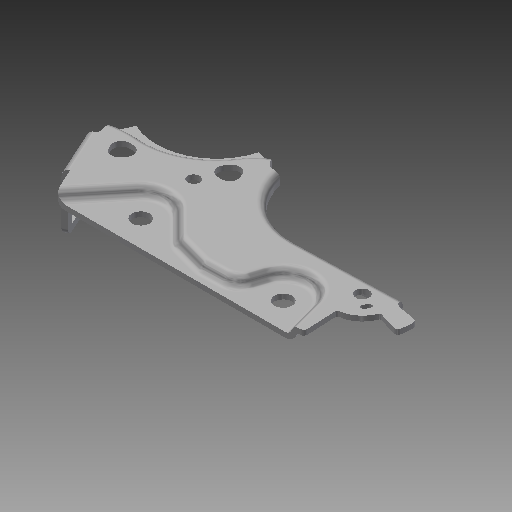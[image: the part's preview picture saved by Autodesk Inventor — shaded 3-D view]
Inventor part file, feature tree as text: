
AUTODESK INVENTOR PART (.ipt)
format: ipt  version: 2019 (Build 230136000, 136)  size: 795,648 bytes
history: native  units: mm
features: fillet x22, sketch x18, extrude x16, hole x2, plane x1, chamfer x1, other x1
ambient origin geometry x8: Origin, YZ Plane, XZ Plane, XY Plane, X Axis, Y Axis, Z Axis, Center Point
bodies: Solid1 (feature_tree)
feature tree (61):
  extrude  "Extrusion1"  Depth=24.072582mm
  fillet  "Fillet1"  Radius=40.0mm
  fillet  "Fillet2"  Radius=94.598888mm
  fillet  "Fillet3"  Radius=160.198557mm
  extrude  "Extrusion2"  Depth=96.114965mm
  fillet  "Fillet4"  Radius=10.045152mm
  extrude  "Extrusion3"  Depth=20.365459mm
  extrude  "Extrusion7"  Depth=45.416983mm
  extrude  "Extrusion8"  Depth=3.0mm
  fillet  "Fillet11"  Radius=22.488064mm
  fillet  "Fillet12"  Radius=151.434268mm
  fillet  "Fillet13"  Radius=3.0mm
  extrude  "Extrusion9"  Depth=2.0mm
  extrude  "Extrusion10"  Depth=4.0mm
  extrude  "Extrusion11"  Depth=79.045157mm
  fillet  "Fillet14"  Radius=32.0mm
  fillet  "Fillet15"  Radius=32.0mm
  fillet  "Fillet16"  Radius=60.0mm
  fillet  "Fillet18"  Radius=80.0mm
  extrude  "Extrusion12"  Depth=10.0mm
  fillet  "Fillet19"  Radius=83.0mm
  fillet  "Fillet20"  Radius=24.0mm
  fillet  "Fillet21"  Radius=95.0mm
  fillet  "Fillet22"  Radius=52.768526mm
  fillet  "Fillet23"  Radius=43.0mm
  extrude  "Extrusion13"  Depth=10.79818mm
  fillet  "Fillet25"  Radius=5.0mm
  extrude  "Extrusion14"  Depth=3.0mm
  fillet  "Fillet26"  Radius=21.0mm
  fillet  "Fillet27"  Radius=44.5mm
  fillet  "Fillet28"  Radius=3.0mm
  plane  "Work Plane2"
  hole  "Hole1"  [1 undecoded]
  extrude  "Extrusion15"  Depth=1.0mm
  extrude  "Extrusion16"  Depth=3.0mm
  extrude  "Extrusion17"  Depth=3.0mm
  fillet  "Fillet29"  Radius=3.0mm
  chamfer  "Chamfer1"  Distance=3.0mm
  hole  "Hole3"  [1 undecoded]
  extrude  "Extrusion18"  Depth=4.0mm
  fillet  "Fillet30"  Radius=2.0mm
  extrude  "Extrusion19"  Depth=10.0mm
  sketch  "Sketch2"  dims[d0=36.0mm d1=24.072582mm d2=40.0mm d3=94.598888mm d4=160.198557mm]
  sketch  "Sketch3"  dims[d5=72.17844mm d6=96.114965mm d7=10.045152mm]
  sketch  "Sketch4"  dims[d9=12.319886mm d10=20.365459mm]
  sketch  "Sketch9"  dims[d11=19.108732mm d12=45.416983mm]
  sketch  "Sketch10"  dims[d15=19.938804mm d16=17.317927mm d18=22.488064mm d19=151.434268mm d20=3.0mm d21=0.0mm]
  sketch  "Sketch11"  dims[d22=25.0mm d23=2.0mm]
  sketch  "Sketch12"  dims[d24=4.0mm d25=79.045157mm]
  sketch  "Sketch13"  dims[d26=33.682036mm d28=79.045157mm d29=32.0mm d30=32.0mm d33=60.0mm d34=80.0mm]
  sketch  "Sketch14"  dims[d36=5.0mm d37=0.0mm d38=10.0mm d41=83.0mm d42=24.0mm d43=95.0mm d45=52.768526mm d46=43.0mm]
  sketch  "Sketch15"  dims[d47=27.664247mm d48=10.79818mm d51=5.0mm d52=0.0mm]
  sketch  "Sketch16"  dims[d55=6.5mm d73=3.0mm d74=21.0mm d75=44.5mm d76=3.0mm d77=0.0mm]
  other  "Work Axis1"
  sketch  "Sketch17"  dims[d78=3.0mm d79=0.0mm d80=4.0mm]
  sketch  "Sketch18"  dims[d81=7.0mm d82=1.0mm]
  sketch  "Sketch19"  dims[d83=3.0mm d84=43.0mm]
  sketch  "Sketch21"  dims[d85=4.0mm d86=0.0mm d87=3.0mm d88=3.0mm d89=3.0mm d90=0.0mm]
  sketch  "Sketch22"  dims[d92=3.0mm d93=0.0mm d94=4.0mm]
  sketch  "Sketch23"  dims[d95=7.0mm d96=1.0mm d97=4.0mm d99=2.0mm]
  sketch  "Sketch24"  dims[d100=0.0mm d101=5.0mm d102=8.0mm d103=3.0mm d104=0.0mm d105=4.0mm d106=1.0mm d107=15.0mm d108=5.0mm d109=2.5mm d110=32.0mm d111=30.0mm d112=4.0mm d113=6.0mm d114=4.5mm d115=4.5mm d116=3.0mm d117=0.0mm d119=1.0mm d120=2.0mm d121=10.0mm d122=10.0mm d123=0.0mm d124=4.0mm d125=4.0mm d126=1.0mm d127=90.0deg d128=10.5mm d129=6.0mm d130=4.0mm d131=2.0mm d132=90.0deg d133=8.0mm d134=20.594885mm d135=10.0mm d136=0.0mm d137=41.737765mm d138=35.0mm d139=53.0mm d140=7.1mm d143=10.0mm d144=0.0mm d145=35.12571mm d146=48.872217mm d156=16.0mm d157=16.0mm d158=2.92523mm d159=0.478162mm d160=0.79648mm d161=4.583492mm d162=10.0mm d163=0.0mm d164=1.0mm d165=1.0mm d166=2.0mm d167=45.0deg d170=118.826923mm d171=15.0deg d172=5.759587mm d173=144.984386mm d174=57.885142mm d175=8.0mm d176=6.0mm d177=4.0mm d178=2.0mm d179=90.0deg d180=8.0mm d181=20.594885mm d182=144.984386mm d183=57.885142mm d184=60.0mm d185=30.0mm d186=10.0mm d187=0.0mm d188=2.0mm d189=3.0mm d190=2.5mm d191=10.0mm d192=0.0mm]
note: 2 required parameter values undecoded (feature->parameter linkage not recoverable at this tier; creation-order binding heuristic only, values carry confidence <= 0.55)
